# Revit family: Genelec_4010
name_source: partatom
category: Generic Models
units: mm (PartAtom-declared; Revit-internal decimal feet)

## family parameters
Always vertical = No
Can host rebar = No
Cut with Voids When Loaded = No
Maintain Annotation Orientation = No
Part Type = Normal
Room Calculation Point = Yes
Round Connector Dimension = Use Diameter
Shared = No
Work Plane-Based = No

## types (2) — shared parameters
Accuracy of Frequency Response = ± 2.5 dB (74 Hz - 20 kHz)
Acoustic Axis = 107
BIMobject category = Audio Electronics
Color = RAL_9018_Papyrus White
Connections = 1 x Euroblock Analog Input
1 x Euroblock Analog Input
1 x Euroblock Analog Input
1 x Euroblock Analog Input
Default Elevation = 1200 mm
Depth = 115 mm
Description = The 4010A Active Installation Loudspeaker offers in compact dimensions excellent clarity, reliability and adaptability as its larger 4000 series family members. 
The 4010A Active Installation Loudspeaker offers in compact dimensions excellent clarity, reliability and adaptability as its larger 4000 series family members. 
The 4010A Active Installation Loudspeaker offers in compact dimensions excellent clarity, reliability and adaptability as its larger 4000 series family members.
Dispersion Angle = H 130° V 110°
Driver Dimensions = ⌀ 76 mm Woofer+ ⌀ 19 mm Tweeter
Export Type to IFC As = IfcAudioVisualApplianceType
Finish Type = Die cast aluminium
Frequency Response = 67 Hz - 25 kHz (-6 dB)
Height = 181 mm
IFC Classification = Electric Appliance
IFC Name = 4010A
Line Drawing = https://assets.ctfassets.net
Mains Voltage = 100-240 VAC 50/60Hz
Manufacturer = GENELEC
Manufacturer Country = Finland
Max. short term sine wave acoustic output  on axis in half space, averaged from 100Hz to 3 kHz = ≥ 96 dB SPL
Maximum long term RMS acoustic output in same conditions with IEC weighted noise (limited by driver unit protection circuit) = ≥ 91 dB SPL
Model = 4010A
Model Description = Active Installation Speaker
Model Image = https://images.ctfassets.net
Model Name = 4010A
Mounting Type = Integrated mounts incl. 3/8 in mic stand and integrated rear-panel support points for mounting, extensive range of accessories available separately. Package includes mount: 8010-410B/W
Power Consumption = 30 W
Power consumption Idle = ≤5 W
Power consumption Standby = ≤0.5 W (ISS Active)
Price List Description = Compact aluminium cabinet with tightly controlled directivity and minimum diffraction for excellent performance. Both drivers have metal protection grilles, with 76 mm (3 in) LF and 19 mm (3/4 in)  HF transducers. Integrated crossover and Class D amplifiers 25 W + 25 W. Max. SPL 96 dB, frequency response 67 Hz - 25 kHz (- 6 dB). 

Room response controls on rear panel to compensate the placement and room effects. On-Off switch on the rear panel.   Dimensions: H 181 x W 121 x D 115 mm, weight 1,5 kg.
Product Family = Installation Speaker
Product Group = 4000 Series Installation Speakers
Self-generated Noise = ≤5 dB
Type IFC Predefined Type = SPEAKER
Type Image = <None>
URL = https://www.genelec.com
Uniclass 2.0 Description = Sound Amplifiers
Weight = 1.5
Width = 121 mm

## per-type parameters (varying)
| type | Horizontal Visibility | Vertical Visibility |
| 4010 Vertical | No | Yes |
| 4010 Horizontal | Yes | No |

## geometry (parser evidence)
native form markers: Sweep x2
no freeform markers — native parametric forms only
